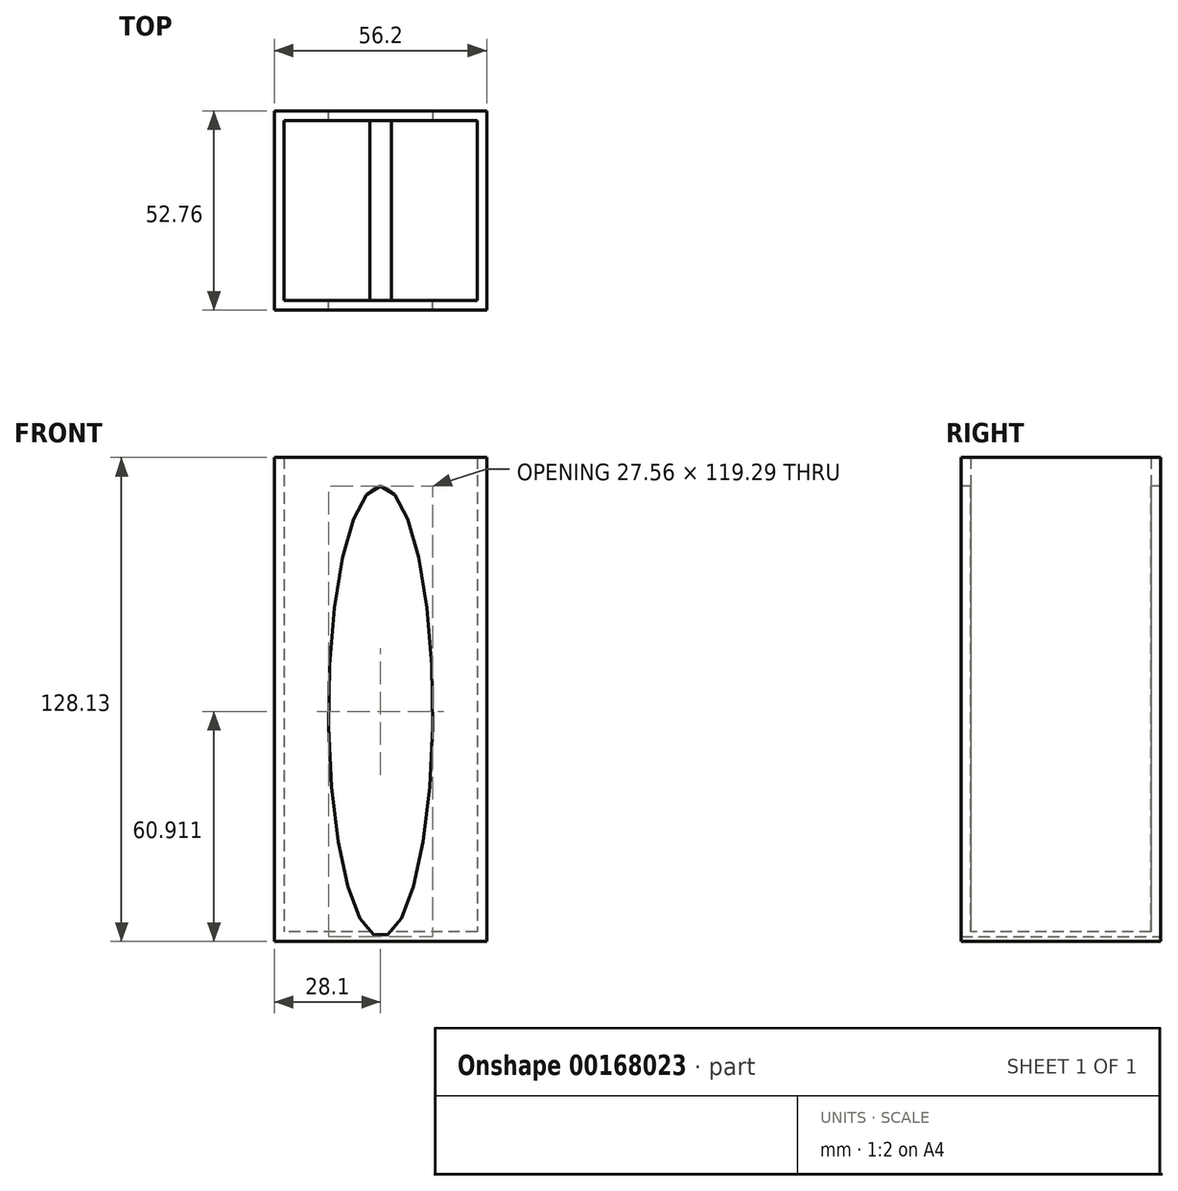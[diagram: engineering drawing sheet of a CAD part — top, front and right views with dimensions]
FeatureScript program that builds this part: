
annotation { "Feature Type Name" : "Feature", "Feature Type Description" : "" }
export const myFeature = defineFeature(function(context is Context, id is Id, definition is map)
    precondition{}
    {
        {
            var Q0;
            Q0=qCreatedBy(makeId("Top.planeOp"),FACE);
            var sketch = newSketch(context, id + "F0", { "sketchPlane" : qUnion([Q0])});
            skLineSegment(sketch, "E0.bottom", {"start": v(28.1, 26.38) * mm, "end": v(-28.1, 26.38) * mm});
            skLineSegment(sketch, "E0.top", {"start": v(28.1, -26.38) * mm, "end": v(-28.1, -26.38) * mm});
            skLineSegment(sketch, "E0.left", {"start": v(28.1, 26.38) * mm, "end": v(28.1, -26.38) * mm});
            skLineSegment(sketch, "E0.right", {"start": v(-28.1, 26.38) * mm, "end": v(-28.1, -26.38) * mm});
            skPoint(sketch, "E0.middle", {"position": v(0, 0) * mm});
            skSolve(sketch);
        }
        {
            var Q0;
            Q0 = qSketchRegion(id + "F0", true);
            extrude(context, id + "F1", {"entities" : qUnion([Q0]), "depth" : 128.13 * mm});
        }
        {
            var Q0;
            Q0=makeQuery(id+"F1.opExtrude","CAP_FACE",FACE,{"disambiguationData":[OSD([sQuery(id+"F0.wireOp",EDGE,"E0.bottom"),sQuery(id+"F0.wireOp",EDGE,"E0.top"),sQuery(id+"F0.wireOp",EDGE,"E0.left"),sQuery(id+"F0.wireOp",EDGE,"E0.right")])],"isStart":false});
            shell(context, id + "F2", {"entities" : qUnion([Q0]), "thickness" : 2.54 * mm});
        }
        {
            var Q0;
            Q0=makeQuery(id+"F1.opExtrude","SWEPT_FACE",FACE,{"disambiguationData":[OSD([sQuery(id+"F0.wireOp",EDGE,"E0.top")])]});
            var sketch = newSketch(context, id + "F3", { "sketchPlane" : qUnion([Q0])});
            skEllipse(sketch, "E1", {"center": v(0, 60.91) * mm, "majorRadius": 59.64 * mm, "minorRadius": 13.78 * mm, "majorAxis": v(0, 1)});
            skSolve(sketch);
        }
        {
            var Q0;
            Q0 = qSketchRegion(id + "F3", true);
            extrude(context, id + "F4", {"entities" : qUnion([Q0]), "operationType" : NewBodyOperationType.REMOVE, "oppositeDirection" : true, "depth" : 87.94 * mm});
        }
        {
            var Q0;
            Q0 = qSketchRegion(id + "F3", true);
            extrude(context, id + "F5", {"entities" : qUnion([Q0]), "depth" : 25.4 * mm});
        }
        {
            var Q0;
            Q0=makeQuery(id+"F5.opExtrude","CAP_FACE",FACE,{"disambiguationData":[OSD([sQuery(id+"F3.wireOp",EDGE,"E1")])],"isStart":false});
            extrude(context, id + "F6", {"entities" : qUnion([Q0]), "operationType" : NewBodyOperationType.REMOVE, "oppositeDirection" : true, "depth" : 25.4 * mm});
        }
    });
